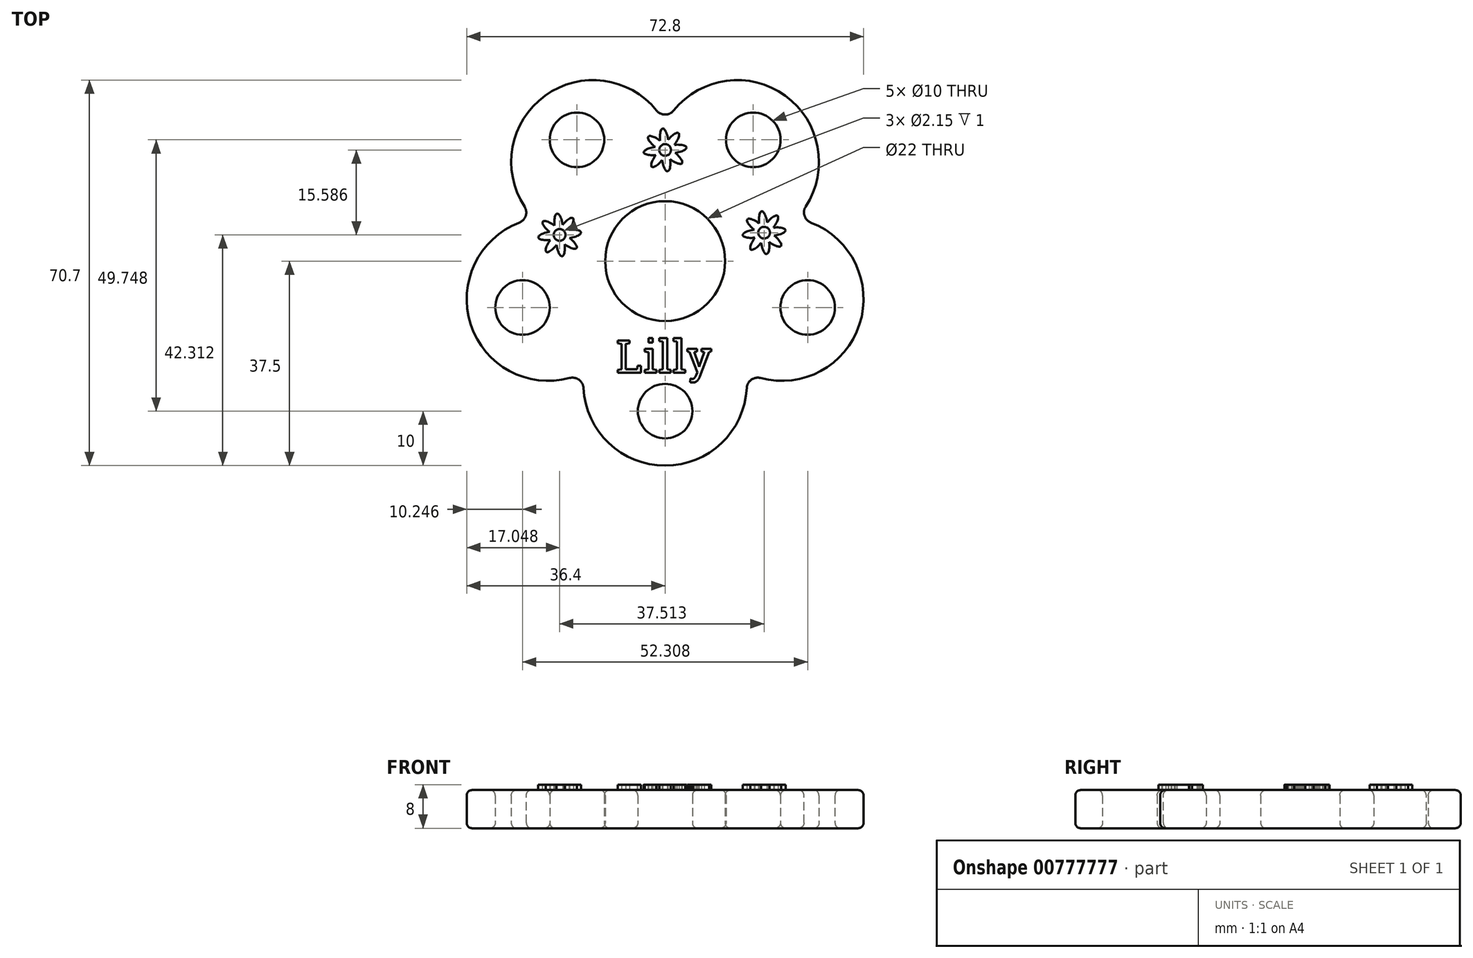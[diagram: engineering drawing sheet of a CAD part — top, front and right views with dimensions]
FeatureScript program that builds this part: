
annotation { "Feature Type Name" : "Feature", "Feature Type Description" : "" }
export const myFeature = defineFeature(function(context is Context, id is Id, definition is map)
    precondition{}
    {
        {
            var Q0;
            Q0=qCreatedBy(makeId("Top.planeOp"),FACE);
            var sketch = newSketch(context, id + "F0", { "sketchPlane" : qUnion([Q0])});
            skCircle(sketch, "E0.cCircle", {"center": v(0, 0) * mm, "radius": 22.5 * mm, "construction": true});
            skPoint(sketch, "E0.0.midPoint", {"position": v(13.23, 18.2) * mm});
            skArc(sketch, "E1", {"start": v(0, 25.28) * mm, "mid": v(-22.04, 30.34) * mm, "end": v(-24.04, 7.81) * mm});
            skArc(sketch, "E2", {"start": v(24.04, 7.81) * mm, "mid": v(22.04, 30.34) * mm, "end": v(0, 25.28) * mm});
            skArc(sketch, "E3", {"start": v(14.86, -20.45) * mm, "mid": v(35.66, -11.59) * mm, "end": v(24.04, 7.81) * mm});
            skArc(sketch, "E4", {"start": v(-14.86, -20.45) * mm, "mid": v(0, -37.5) * mm, "end": v(14.86, -20.45) * mm});
            skArc(sketch, "E5", {"start": v(-24.04, 7.81) * mm, "mid": v(-35.66, -11.59) * mm, "end": v(-14.86, -20.45) * mm});
            skCircle(sketch, "E6", {"center": v(0, 0) * mm, "radius": 25.28 * mm, "construction": true});
            skCircle(sketch, "E7", {"center": v(0, 0) * mm, "radius": 11 * mm});
            skCircle(sketch, "E8", {"center": v(-16.16, 22.25) * mm, "radius": 5 * mm});
            skCircle(sketch, "E9", {"center": v(16.16, 22.25) * mm, "radius": 5 * mm});
            skCircle(sketch, "E10", {"center": v(26.15, -8.5) * mm, "radius": 5 * mm});
            skCircle(sketch, "E11", {"center": v(0, -27.5) * mm, "radius": 5 * mm});
            skCircle(sketch, "E12", {"center": v(-26.15, -8.5) * mm, "radius": 5 * mm});
            skCircle(sketch, "E13", {"center": v(0, 0) * mm, "radius": 27.5 * mm, "construction": true});
            skLineSegment(sketch, "E14", {"start": v(0, 0) * mm, "end": v(0, 61.86) * mm, "construction": true});
            skLineSegment(sketch, "E15", {"start": v(0, 0) * mm, "end": v(37, 50.93) * mm, "construction": true});
            skLineSegment(sketch, "E16", {"start": v(0, 0) * mm, "end": v(73.63, -23.92) * mm, "construction": true});
            skLineSegment(sketch, "E17", {"start": v(0, 0) * mm, "end": v(0, -32.5) * mm, "construction": true});
            skLineSegment(sketch, "E18", {"start": v(0, 0) * mm, "end": v(-65.18, -21.18) * mm, "construction": true});
            skLineSegment(sketch, "E19", {"start": v(0, 0) * mm, "end": v(-33.66, 46.32) * mm, "construction": true});
            skSolve(sketch);
        }
        {
            var Q0;
            Q0=qSketchRegion(id+"F0",true);
            extrude(context, id + "F1", {"entities" : qUnion([Q0]), "depth" : 7 * mm, "offsetDistance" : 25.4 * mm});
        }
        {
            var Q0;
            Q0=makeQuery(id+"F1.opExtrude","SWEPT_EDGE",EDGE,{"disambiguationData":[OSD([sQuery(id+"F0.wireOp",EDGE,"E3"),sQuery(id+"F0.wireOp",EDGE,"E4")])]});
            var Q1;
            Q1=makeQuery(id+"F1.opExtrude","SWEPT_EDGE",EDGE,{"disambiguationData":[OSD([sQuery(id+"F0.wireOp",EDGE,"E2"),sQuery(id+"F0.wireOp",EDGE,"E3")])]});
            var Q2;
            Q2=makeQuery(id+"F1.opExtrude","SWEPT_EDGE",EDGE,{"disambiguationData":[OSD([sQuery(id+"F0.wireOp",EDGE,"E1"),sQuery(id+"F0.wireOp",EDGE,"E2")])]});
            var Q3;
            Q3=makeQuery(id+"F1.opExtrude","SWEPT_EDGE",EDGE,{"disambiguationData":[OSD([sQuery(id+"F0.wireOp",EDGE,"E1"),sQuery(id+"F0.wireOp",EDGE,"E5")])]});
            var Q4;
            Q4=makeQuery(id+"F1.opExtrude","SWEPT_EDGE",EDGE,{"disambiguationData":[OSD([sQuery(id+"F0.wireOp",EDGE,"E4"),sQuery(id+"F0.wireOp",EDGE,"E5")])]});
            fillet(context, id + "F2", {"entities" : qUnion([Q0, Q1, Q2, Q3, Q4]), "radius" : 2 * mm, "tangentPropagation" : true, "allowEdgeOverflow" : false});
        }
        {
            var Q0;
            Q0=makeQuery(id+"F1.opExtrude","CAP_FACE",FACE,{"disambiguationData":[OSD([sQuery(id+"F0.wireOp",EDGE,"E1"),sQuery(id+"F0.wireOp",EDGE,"E2"),sQuery(id+"F0.wireOp",EDGE,"E3"),sQuery(id+"F0.wireOp",EDGE,"E4"),sQuery(id+"F0.wireOp",EDGE,"E5"),sQuery(id+"F0.wireOp",EDGE,"E7"),sQuery(id+"F0.wireOp",EDGE,"E8"),sQuery(id+"F0.wireOp",EDGE,"E9"),sQuery(id+"F0.wireOp",EDGE,"E10"),sQuery(id+"F0.wireOp",EDGE,"E11"),sQuery(id+"F0.wireOp",EDGE,"E12")])],"isStart":false});
            var Q1;
            Q1=makeQuery(id+"F1.opExtrude","CAP_FACE",FACE,{"disambiguationData":[OSD([sQuery(id+"F0.wireOp",EDGE,"E1"),sQuery(id+"F0.wireOp",EDGE,"E2"),sQuery(id+"F0.wireOp",EDGE,"E3"),sQuery(id+"F0.wireOp",EDGE,"E4"),sQuery(id+"F0.wireOp",EDGE,"E5"),sQuery(id+"F0.wireOp",EDGE,"E7"),sQuery(id+"F0.wireOp",EDGE,"E8"),sQuery(id+"F0.wireOp",EDGE,"E9"),sQuery(id+"F0.wireOp",EDGE,"E10"),sQuery(id+"F0.wireOp",EDGE,"E11"),sQuery(id+"F0.wireOp",EDGE,"E12")])],"isStart":true});
            fillet(context, id + "F3", {"entities" : qUnion([Q0, Q1]), "radius" : 1 * mm, "tangentPropagation" : true, "allowEdgeOverflow" : false});
        }
        {
            var Q0;
            Q0=makeQuery(id+"F1.opExtrude","CAP_FACE",FACE,{"disambiguationData":[OSD([sQuery(id+"F0.wireOp",EDGE,"E1"),sQuery(id+"F0.wireOp",EDGE,"E2"),sQuery(id+"F0.wireOp",EDGE,"E3"),sQuery(id+"F0.wireOp",EDGE,"E4"),sQuery(id+"F0.wireOp",EDGE,"E5"),sQuery(id+"F0.wireOp",EDGE,"E7"),sQuery(id+"F0.wireOp",EDGE,"E8"),sQuery(id+"F0.wireOp",EDGE,"E9"),sQuery(id+"F0.wireOp",EDGE,"E10"),sQuery(id+"F0.wireOp",EDGE,"E11"),sQuery(id+"F0.wireOp",EDGE,"E12")])],"isStart":false});
            var sketch = newSketch(context, id + "F4", { "sketchPlane" : qUnion([Q0])});
            skText(sketch, "E20", { "text": "Lilly", "fontName": "RobotoSlab-Regular.ttf"});
            skEllipticalArc(sketch, "E21", {});
            skEllipticalArc(sketch, "E22.1.0", {});
            skEllipticalArc(sketch, "E22.2.0", {});
            skEllipticalArc(sketch, "E22.3.0", {});
            skEllipticalArc(sketch, "E22.4.0", {});
            skEllipticalArc(sketch, "E22.5.0", {});
            skEllipticalArc(sketch, "E22.6.0", {});
            skEllipticalArc(sketch, "E22.7.0", {});
            skPoint(sketch, "E22.center", {"position": v(0, 20.4) * mm});
            skPoint(sketch, "E23.orphan", {"position": v(-1.52, 20.99) * mm});
            skPoint(sketch, "E24.orphan", {"position": v(-0.88, 21.76) * mm});
            skPoint(sketch, "E25.orphan", {"position": v(-0.66, 21.89) * mm});
            skPoint(sketch, "E26.orphan", {"position": v(0.34, 21.99) * mm});
            skPoint(sketch, "E27.orphan", {"position": v(-1.6, 20.74) * mm});
            skPoint(sketch, "E28.orphan", {"position": v(-1.37, 19.51) * mm});
            skPoint(sketch, "E29.orphan", {"position": v(-1.49, 19.74) * mm});
            skPoint(sketch, "E30.orphan", {"position": v(-0.59, 18.88) * mm});
            skPoint(sketch, "E31.orphan", {"position": v(0.66, 18.9) * mm});
            skPoint(sketch, "E32.orphan", {"position": v(0.88, 19.03) * mm});
            skPoint(sketch, "E33.orphan", {"position": v(1.6, 20.06) * mm});
            skPoint(sketch, "E34.orphan", {"position": v(1.37, 21.28) * mm});
            skPoint(sketch, "E35.orphan", {"position": v(0.59, 21.92) * mm});
            skCircle(sketch, "E36", {"center": v(0, 20.4) * mm, "radius": 1.07 * mm});
            skEllipticalArc(sketch, "E37", {});
            skEllipticalArc(sketch, "E38.1.0", {});
            skEllipticalArc(sketch, "E38.2.0", {});
            skEllipticalArc(sketch, "E38.3.0", {});
            skEllipticalArc(sketch, "E38.4.0", {});
            skEllipticalArc(sketch, "E38.5.0", {});
            skEllipticalArc(sketch, "E38.6.0", {});
            skEllipticalArc(sketch, "E38.7.0", {});
            skPoint(sketch, "E38.center", {"position": v(-19.35, 4.81) * mm});
            skPoint(sketch, "E39.orphan", {"position": v(-20.87, 5.4) * mm});
            skPoint(sketch, "E40.orphan", {"position": v(-20.24, 6.18) * mm});
            skPoint(sketch, "E41.orphan", {"position": v(-20, 6.3) * mm});
            skPoint(sketch, "E42.orphan", {"position": v(-19.01, 6.4) * mm});
            skPoint(sketch, "E43.orphan", {"position": v(-20.94, 5.15) * mm});
            skPoint(sketch, "E44.orphan", {"position": v(-20.72, 3.93) * mm});
            skPoint(sketch, "E45.orphan", {"position": v(-20.84, 4.15) * mm});
            skPoint(sketch, "E46.orphan", {"position": v(-19.94, 3.3) * mm});
            skPoint(sketch, "E47.orphan", {"position": v(-18.7, 3.32) * mm});
            skPoint(sketch, "E48.orphan", {"position": v(-18.47, 3.45) * mm});
            skPoint(sketch, "E49.orphan", {"position": v(-17.76, 4.47) * mm});
            skPoint(sketch, "E50.orphan", {"position": v(-17.99, 5.7) * mm});
            skPoint(sketch, "E51.orphan", {"position": v(-18.76, 6.33) * mm});
            skCircle(sketch, "E52", {"center": v(-19.35, 4.81) * mm, "radius": 1.07 * mm});
            skEllipticalArc(sketch, "E53", {});
            skEllipticalArc(sketch, "E54.1.0", {});
            skEllipticalArc(sketch, "E54.2.0", {});
            skEllipticalArc(sketch, "E54.3.0", {});
            skEllipticalArc(sketch, "E54.4.0", {});
            skEllipticalArc(sketch, "E54.5.0", {});
            skEllipticalArc(sketch, "E54.6.0", {});
            skEllipticalArc(sketch, "E54.7.0", {});
            skPoint(sketch, "E54.center", {"position": v(18.16, 5.23) * mm});
            skPoint(sketch, "E55.orphan", {"position": v(16.64, 5.82) * mm});
            skPoint(sketch, "E56.orphan", {"position": v(17.28, 6.6) * mm});
            skPoint(sketch, "E57.orphan", {"position": v(17.5, 6.72) * mm});
            skPoint(sketch, "E58.orphan", {"position": v(18.5, 6.82) * mm});
            skPoint(sketch, "E59.orphan", {"position": v(16.57, 5.57) * mm});
            skPoint(sketch, "E60.orphan", {"position": v(16.8, 4.34) * mm});
            skPoint(sketch, "E61.orphan", {"position": v(16.67, 4.57) * mm});
            skPoint(sketch, "E62.orphan", {"position": v(17.57, 3.7) * mm});
            skPoint(sketch, "E63.orphan", {"position": v(18.82, 3.74) * mm});
            skPoint(sketch, "E64.orphan", {"position": v(19.04, 3.86) * mm});
            skPoint(sketch, "E65.orphan", {"position": v(19.75, 4.89) * mm});
            skPoint(sketch, "E66.orphan", {"position": v(19.53, 6.11) * mm});
            skPoint(sketch, "E67.orphan", {"position": v(18.75, 6.74) * mm});
            skCircle(sketch, "E68", {"center": v(18.16, 5.23) * mm, "radius": 1.07 * mm});
            const initialGuessF4  = {"E20": [-0.00896, -0.02048, 1, 0, 0.006], "E21": [0.0010247566278231382, 0.02166222113838485, 0.6140089271210712, 0.7892990798269254, 0.0023157442023888897, 0.0007414824988597866, 4.775112420753962, 1.4962821796103536], "E22.1.0": [-0.00016934392095610713, 0.022016544682995458, -0.1239488556535351, 0.9922886078063071, 0.0023157442023888897, 0.0007414824988597866, 4.7751124207539615, 1.4962821796103567], "E22.2.0": [-0.0012642450975447021, 0.021422732668663284, -0.7892990798269255, 0.614008927121071, 0.0023157442023888897, 0.0007414824988597866, 4.775112420753961, 1.4962821796103531], "E22.3.0": [-0.0016185686421553084, 0.02022863211988404, -0.9922886078063071, -0.12394885565353492, 0.0023157442023888897, 0.0007414824988597866, 4.775112420753962, 1.496282179610354], "E22.4.0": [-0.0010247566278231385, 0.019133730943295447, -0.614008927121071, -0.7892990798269255, 0.0023157442023888897, 0.0007414824988597866, 4.7751124207539615, 1.4962821796103547], "E22.5.0": [0.00016934392095610713, 0.01877940739868484, 0.12394885565353497, -0.9922886078063071, 0.0023157442023888897, 0.0007414824988597866, 4.77511242075396, 1.4962821796103551], "E22.6.0": [0.0012642450975447021, 0.01937321941301701, 0.7892990798269254, -0.6140089271210711, 0.0023157442023888897, 0.0007414824988597866, 4.775112420753961, 1.4962821796103563], "E22.7.0": [0.0016185686421553084, 0.020567319961796258, 0.9922886078063071, 0.12394885565353492, 0.0023157442023888897, 0.0007414824988597866, 4.77511242075396, 1.4962821796103547], "E37": [-0.01832736750656251, 0.006076403150645358, 0.6140089271210712, 0.7892990798269254, 0.0023157442023888897, 0.0007414824988597866, 4.7751124207539615, 1.4962821796103527], "E38.1.0": [-0.019521468055341756, 0.006430726695255965, -0.1239488556535351, 0.9922886078063071, 0.0023157442023888897, 0.0007414824988597866, 4.7751124207539615, 1.4962821796103567], "E38.2.0": [-0.020616369231930352, 0.005836914680923792, -0.7892990798269255, 0.614008927121071, 0.0023157442023888897, 0.0007414824988597866, 4.775112420753961, 1.4962821796103531], "E38.3.0": [-0.02097069277654096, 0.004642814132144547, -0.9922886078063071, -0.12394885565353492, 0.0023157442023888897, 0.0007414824988597866, 4.775112420753963, 1.4962821796103538], "E38.4.0": [-0.02037688076220879, 0.0035479129555559545, -0.614008927121071, -0.7892990798269255, 0.0023157442023888897, 0.0007414824988597866, 4.775112420753961, 1.496282179610355], "E38.5.0": [-0.019182780213429545, 0.0031935894109453478, 0.12394885565353497, -0.9922886078063071, 0.0023157442023888897, 0.0007414824988597866, 4.77511242075396, 1.4962821796103551], "E38.6.0": [-0.018087879036840948, 0.0037874014252775178, 0.7892990798269254, -0.6140089271210711, 0.0023157442023888897, 0.0007414824988597866, 4.775112420753961, 1.4962821796103551], "E38.7.0": [-0.01773355549223034, 0.004981501974056765, 0.9922886078063071, 0.12394885565353492, 0.0023157442023888897, 0.0007414824988597866, 4.775112420753958, 1.4962821796103551], "E53": [0.019185944400784024, 0.00649146601261529, 0.6140089271210712, 0.7892990798269254, 0.0023157442023888897, 0.0007414824988597866, 4.775112420753962, 1.4962821796103538], "E54.1.0": [0.01799184385200478, 0.006845789557225897, -0.1239488556535351, 0.9922886078063071, 0.0023157442023888897, 0.0007414824988597866, 4.7751124207539615, 1.4962821796103567], "E54.2.0": [0.016896942675416183, 0.006251977542893724, -0.7892990798269255, 0.614008927121071, 0.0023157442023888897, 0.0007414824988597866, 4.775112420753961, 1.4962821796103531], "E54.3.0": [0.016542619130805576, 0.005057876994114479, -0.9922886078063071, -0.12394885565353492, 0.0023157442023888897, 0.0007414824988597866, 4.775112420753962, 1.4962821796103538], "E54.4.0": [0.017136431145137746, 0.003962975817525886, -0.614008927121071, -0.7892990798269255, 0.0023157442023888897, 0.0007414824988597866, 4.7751124207539615, 1.496282179610355], "E54.5.0": [0.01833053169391699, 0.0036086522729152793, 0.12394885565353497, -0.9922886078063071, 0.0023157442023888897, 0.0007414824988597866, 4.77511242075396, 1.4962821796103551], "E54.6.0": [0.019425432870505587, 0.004202464287247449, 0.7892990798269254, -0.6140089271210711, 0.0023157442023888897, 0.0007414824988597866, 4.775112420753961, 1.4962821796103565], "E54.7.0": [0.019779756415116194, 0.005396564836026697, 0.9922886078063071, 0.12394885565353492, 0.0023157442023888897, 0.0007414824988597866, 4.77511242075396, 1.4962821796103551]};
            skSetInitialGuess(sketch, initialGuessF4);
            skSolve(sketch);
        }
        {
            var Q0;
            Q0=qSketchRegion(id+"F4",true);
            extrude(context, id + "F5", {"entities" : qUnion([Q0]), "operationType" : NewBodyOperationType.ADD, "depth" : 1 * mm, "offsetDistance" : 25 * mm});
        }
    });
